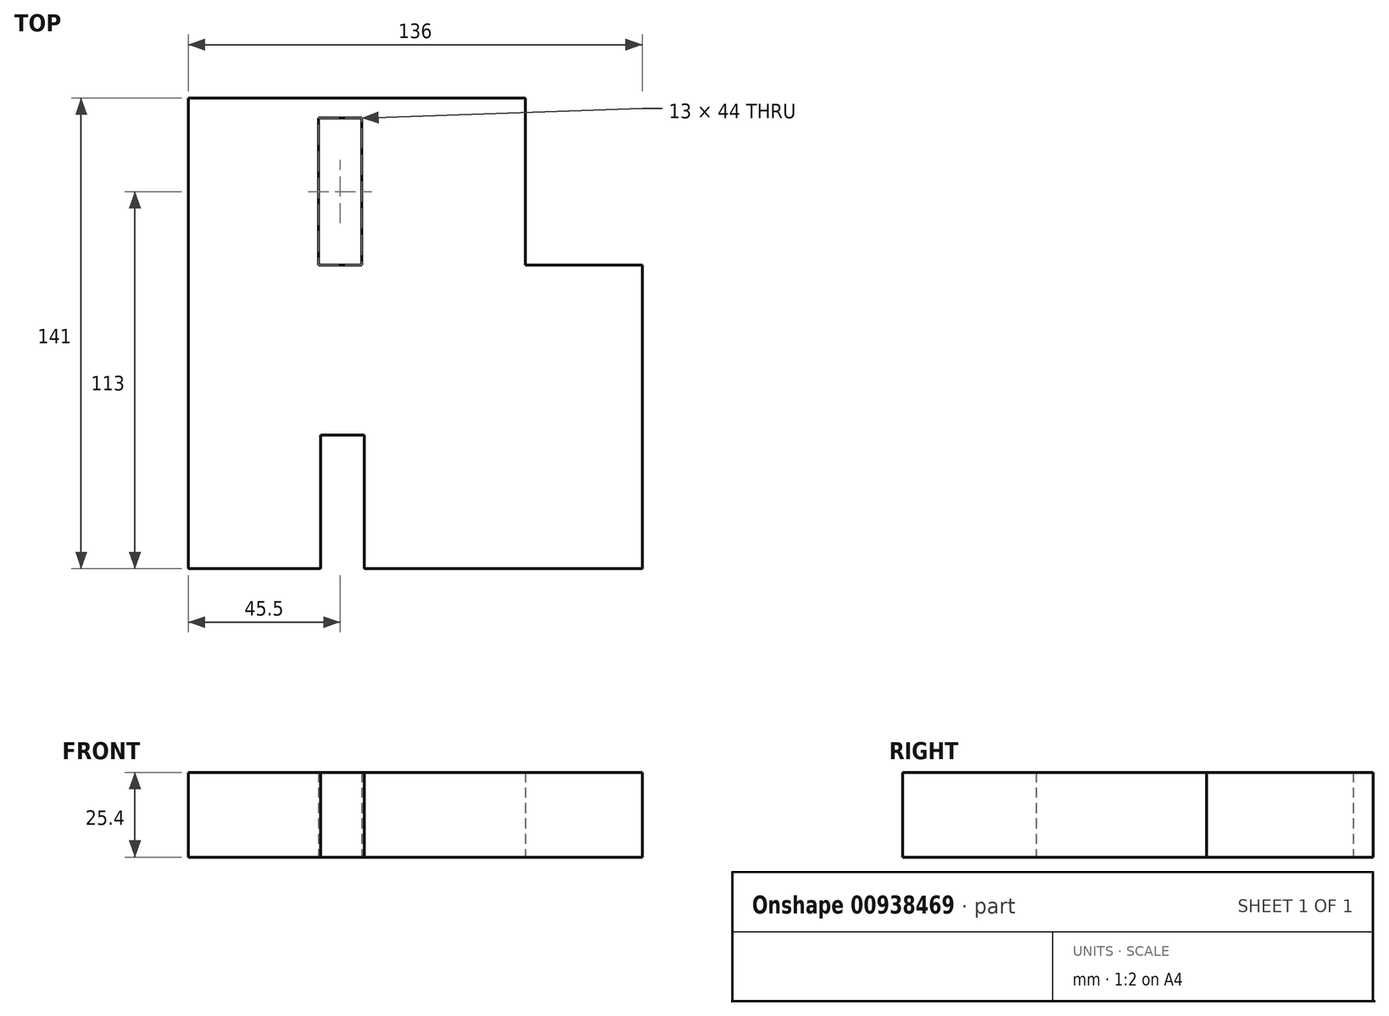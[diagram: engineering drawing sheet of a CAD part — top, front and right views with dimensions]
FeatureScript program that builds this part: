
annotation { "Feature Type Name" : "Feature", "Feature Type Description" : "" }
export const myFeature = defineFeature(function(context is Context, id is Id, definition is map)
    precondition{}
    {
        {
            var Q0;
            Q0=qCreatedBy(makeId("Top.planeOp"),FACE);
            var sketch = newSketch(context, id + "F0", { "sketchPlane" : qUnion([Q0])});
            skLineSegment(sketch, "E0.bottom", {"start": v(33, 70.5) * mm, "end": v(-68, 70.5) * mm});
            skLineSegment(sketch, "E0.top", {"start": v(68, -70.5) * mm, "end": v(-15.31, -70.5) * mm});
            skLineSegment(sketch, "E0.left", {"start": v(68, 20.5) * mm, "end": v(68, -70.5) * mm});
            skLineSegment(sketch, "E0.right", {"start": v(-68, 70.5) * mm, "end": v(-68, -70.5) * mm});
            skPoint(sketch, "E0.middle", {"position": v(0, 0) * mm});
            skLineSegment(sketch, "E1.bottom", {"start": v(-29, 64.5) * mm, "end": v(-16, 64.5) * mm});
            skLineSegment(sketch, "E1.top", {"start": v(-29, 20.5) * mm, "end": v(-16, 20.5) * mm});
            skLineSegment(sketch, "E1.left", {"start": v(-29, 64.5) * mm, "end": v(-29, 20.5) * mm});
            skLineSegment(sketch, "E1.right", {"start": v(-16, 64.5) * mm, "end": v(-16, 20.5) * mm});
            skLineSegment(sketch, "E2.top", {"start": v(33, 20.5) * mm, "end": v(68, 20.5) * mm});
            skLineSegment(sketch, "E2.left", {"start": v(33, 70.5) * mm, "end": v(33, 20.5) * mm});
            skLineSegment(sketch, "E3.top", {"start": v(-28.31, -30.5) * mm, "end": v(-15.31, -30.5) * mm});
            skLineSegment(sketch, "E3.left", {"start": v(-28.31, -70.5) * mm, "end": v(-28.31, -30.5) * mm});
            skLineSegment(sketch, "E3.right", {"start": v(-15.31, -70.5) * mm, "end": v(-15.31, -30.5) * mm});
            skPoint(sketch, "E4.orphan", {"position": v(68, 70.5) * mm});
            skLineSegment(sketch, "E5.trimOffspring", {"start": v(-28.31, -70.5) * mm, "end": v(-68, -70.5) * mm});
            skSolve(sketch);
        }
        {
            var Q0;
            Q0=makeQuery(id+"F0.imprint","IMPRINT",FACE,{"disambiguationData":[TD([[makeQuery(id+"F0.imprint","IMPRINT",EDGE,{"derivedFrom":sQuery(id+"F0.wireOp",EDGE,"E0.bottom")}),1.0]])]});
            extrude(context, id + "F1", {"entities" : qUnion([Q0]), "depth" : 25.4 * mm, "offsetDistance" : 25.4 * mm});
        }
    });
